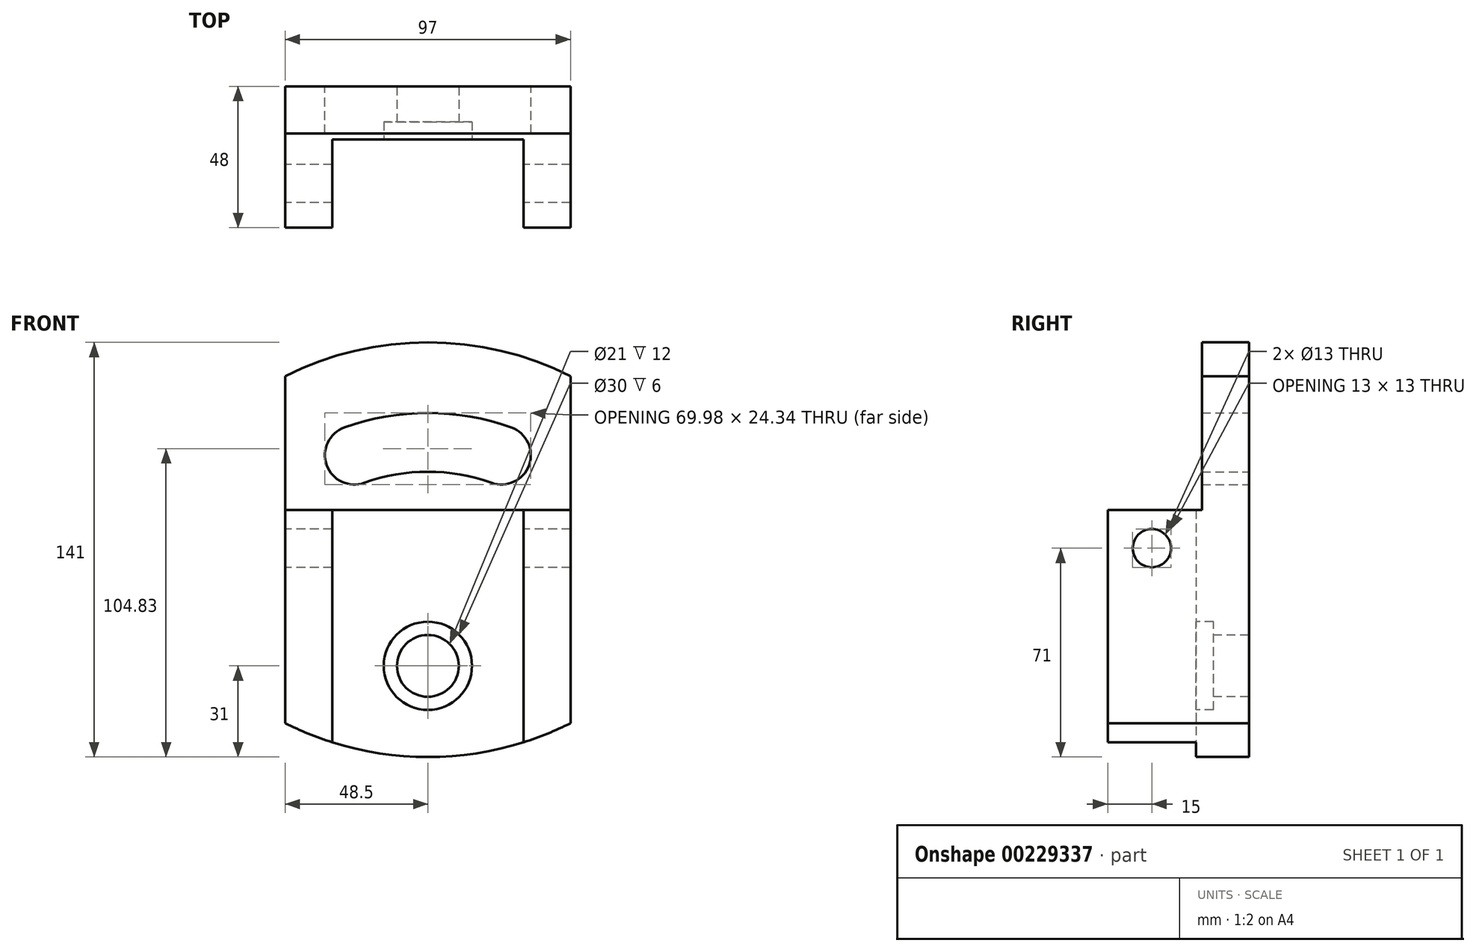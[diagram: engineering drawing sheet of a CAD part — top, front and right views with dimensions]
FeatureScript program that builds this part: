
annotation { "Feature Type Name" : "Feature", "Feature Type Description" : "" }
export const myFeature = defineFeature(function(context is Context, id is Id, definition is map)
    precondition{}
    {
        {
            var Q0;
            Q0=qCreatedBy(makeId("Front.planeOp"),FACE);
            var sketch = newSketch(context, id + "F0", { "sketchPlane" : qUnion([Q0])});
            skLineSegment(sketch, "E0", {"start": v(0, 70.5) * mm, "end": v(0, -70.5) * mm, "construction": true});
            skLineSegment(sketch, "E1", {"start": v(-48.5, 0) * mm, "end": v(48.5, 0) * mm, "construction": true});
            skLineSegment(sketch, "E2.left", {"start": v(48.5, -59) * mm, "end": v(48.5, 59) * mm});
            skLineSegment(sketch, "E2.right", {"start": v(-48.5, -59) * mm, "end": v(-48.5, 59) * mm});
            skPoint(sketch, "E2.middle", {"position": v(0, 0) * mm});
            skArc(sketch, "E3", {"start": v(48.5, 59) * mm, "mid": v(0, 70.5) * mm, "end": v(-48.5, 59) * mm});
            skArc(sketch, "E4", {"start": v(-48.5, -59) * mm, "mid": v(0, -70.5) * mm, "end": v(48.5, -59) * mm});
            skPoint(sketch, "E5.orphan", {"position": v(-48.5, 70.5) * mm});
            skPoint(sketch, "E6.orphan", {"position": v(48.5, 70.5) * mm});
            skPoint(sketch, "E7.orphan", {"position": v(48.5, -70.5) * mm});
            skPoint(sketch, "E2.bottom.end.orphan", {"position": v(-48.5, -70.5) * mm});
            skArc(sketch, "E8.0", {"start": v(25, 32.15) * mm, "mid": v(0, 36.5) * mm, "end": v(-25, 32.15) * mm, "construction": true});
            skArc(sketch, "E9.0.startCap", {"start": v(28.38, 41.56) * mm, "mid": v(34.41, 28.77) * mm, "end": v(21.62, 22.74) * mm});
            skArc(sketch, "E9.0.endCap", {"start": v(-21.62, 22.74) * mm, "mid": v(-34.41, 28.77) * mm, "end": v(-28.38, 41.56) * mm});
            skArc(sketch, "E9.0.left", {"start": v(21.62, 22.74) * mm, "mid": v(0, 26.5) * mm, "end": v(-21.62, 22.74) * mm});
            skArc(sketch, "E9.0.right", {"start": v(28.38, 41.56) * mm, "mid": v(0, 46.5) * mm, "end": v(-28.38, 41.56) * mm});
            skArc(sketch, "E10.0.startCap", {"start": v(28.38, 41.56) * mm, "mid": v(34.41, 28.77) * mm, "end": v(21.62, 22.74) * mm, "construction": true});
            skArc(sketch, "E10.0.endCap", {"start": v(-21.62, 22.74) * mm, "mid": v(-34.41, 28.77) * mm, "end": v(-28.38, 41.56) * mm, "construction": true});
            skArc(sketch, "E10.0.left", {"start": v(21.62, 22.74) * mm, "mid": v(0, 26.5) * mm, "end": v(-21.62, 22.74) * mm, "construction": true});
            skArc(sketch, "E10.0.right", {"start": v(28.38, 41.56) * mm, "mid": v(0, 46.5) * mm, "end": v(-28.38, 41.56) * mm, "construction": true});
            skLineSegment(sketch, "E11", {"start": v(-48.5, 13.5) * mm, "end": v(48.5, 13.5) * mm});
            skSolve(sketch);
        }
        {
            var Q0;
            {var subQ0=sQuery(id+"F0.wireOp",EDGE,"E3");Q0=makeQuery(id+"F0.imprint","IMPRINT",FACE,{"disambiguationData":[TD([[makeQuery(id+"F0.imprint","IMPRINT",EDGE,{"derivedFrom":subQ0}),1.0]])]});}
            extrude(context, id + "F1", {"entities" : qUnion([Q0]), "depth" : 16 * mm});
        }
        {
            var Q0;
            {var subQ0=sQuery(id+"F0.wireOp",EDGE,"E4");Q0=makeQuery(id+"F0.imprint","IMPRINT",FACE,{"disambiguationData":[TD([[makeQuery(id+"F0.imprint","IMPRINT",EDGE,{"derivedFrom":subQ0}),1.0]])]});}
            extrude(context, id + "F2", {"entities" : qUnion([Q0]), "operationType" : NewBodyOperationType.ADD, "depth" : 18 * mm});
        }
        {
            var Q0;
            Q0=makeQuery(id+"F2.opExtrude","CAP_FACE",FACE,{"disambiguationData":[OSD([sQuery(id+"F0.wireOp",EDGE,"E2.left"),sQuery(id+"F0.wireOp",EDGE,"E2.right"),sQuery(id+"F0.wireOp",EDGE,"E4"),sQuery(id+"F0.wireOp",EDGE,"E11")])],"isStart":false});
            var sketch = newSketch(context, id + "F3", { "sketchPlane" : qUnion([Q0])});
            skLineSegment(sketch, "E12", {"start": v(0, 0) * mm, "end": v(0, -70.5) * mm, "construction": true});
            skPoint(sketch, "E13", {"position": v(0, -39.5) * mm});
            skSolve(sketch);
        }
        {
            var Q0;
            Q0=sQuery(id+"F3.wireOp",VERTEX,"E13");
            var Q1;
            Q1=makeQuery(id+"F1.opExtrude","SWEPT_BODY",BODY,{"disambiguationData":[OSD([sQuery(id+"F0.wireOp",EDGE,"E2.left"),sQuery(id+"F0.wireOp",EDGE,"E2.right"),sQuery(id+"F0.wireOp",EDGE,"E3"),sQuery(id+"F0.wireOp",EDGE,"E9.0.startCap"),sQuery(id+"F0.wireOp",EDGE,"E9.0.endCap"),sQuery(id+"F0.wireOp",EDGE,"E9.0.left"),sQuery(id+"F0.wireOp",EDGE,"E9.0.right"),sQuery(id+"F0.wireOp",EDGE,"E11")])]});
            hole(context, id + "F4", {"style" : HoleStyle.C_BORE, "endStyle" : HoleEndStyle.THROUGH, "holeDiameter" : 21 * mm, "cBoreDiameter" : 30 * mm, "cBoreDepth" : 6 * mm, "startFromSketch" : true, "locations" : qUnion([Q0]), "scope" : qUnion([Q1]), "isTappedThrough" : true});
        }
        {
            var Q0;
            Q0=makeQuery(id+"F2.opExtrude","CAP_FACE",FACE,{"disambiguationData":[OSD([sQuery(id+"F0.wireOp",EDGE,"E2.left"),sQuery(id+"F0.wireOp",EDGE,"E2.right"),sQuery(id+"F0.wireOp",EDGE,"E4"),sQuery(id+"F0.wireOp",EDGE,"E11")])],"isStart":false});
            var sketch = newSketch(context, id + "F5", { "sketchPlane" : qUnion([Q0])});
            skLineSegment(sketch, "E14.0", {"start": v(-48.5, -59) * mm, "end": v(-48.5, 13.5) * mm});
            skLineSegment(sketch, "E15.0", {"start": v(-48.5, 13.5) * mm, "end": v(-32.5, 13.5) * mm});
            skLineSegment(sketch, "E16.0", {"start": v(48.5, -59) * mm, "end": v(48.5, 13.5) * mm});
            skArc(sketch, "E17.0", {"start": v(-48.5, -59) * mm, "mid": v(-40.63, -62.57) * mm, "end": v(-32.5, -65.5) * mm});
            skLineSegment(sketch, "E18", {"start": v(-32.5, 13.5) * mm, "end": v(-32.5, -65.5) * mm});
            skLineSegment(sketch, "E19", {"start": v(32.5, 13.5) * mm, "end": v(32.5, -65.5) * mm});
            skArc(sketch, "E20.trimOffspring", {"start": v(32.5, -65.5) * mm, "mid": v(40.63, -62.57) * mm, "end": v(48.5, -59) * mm});
            skLineSegment(sketch, "E21.trimOffspring", {"start": v(32.5, 13.5) * mm, "end": v(48.5, 13.5) * mm});
            skSolve(sketch);
        }
        {
            var Q0;
            Q0 = qSketchRegion(id + "F5", true);
            extrude(context, id + "F6", {"entities" : qUnion([Q0]), "operationType" : NewBodyOperationType.ADD, "depth" : 30 * mm});
        }
        {
            var Q0;
            {var subQ0=sQuery(id+"F0.wireOp",EDGE,"E2.right");Q0=makeQuery(id+"F6.boolean.opBoolean","MERGE",FACE,{"derivedFrom":[makeQuery(id+"F2.boolean.opBoolean","MERGE",FACE,{"derivedFrom":[makeQuery(id+"F1.opExtrude","SWEPT_FACE",FACE,{"disambiguationData":[OSD([subQ0])]}),makeQuery(id+"F2.opExtrude","SWEPT_FACE",FACE,{"disambiguationData":[OSD([subQ0])]})]}),makeQuery(id+"F6.opExtrude","SWEPT_FACE",FACE,{"disambiguationData":[OSD([sQuery(id+"F5.wireOp",EDGE,"E14.0")])]})]});}
            var sketch = newSketch(context, id + "F7", { "sketchPlane" : qUnion([Q0])});
            skPoint(sketch, "E22", {"position": v(33, 0.5) * mm});
            skSolve(sketch);
        }
        {
            var Q0;
            Q0=sQuery(id+"F7.wireOp",VERTEX,"E22");
            var Q1;
            Q1=makeQuery(id+"F1.opExtrude","SWEPT_BODY",BODY,{"disambiguationData":[OSD([sQuery(id+"F0.wireOp",EDGE,"E2.left"),sQuery(id+"F0.wireOp",EDGE,"E2.right"),sQuery(id+"F0.wireOp",EDGE,"E3"),sQuery(id+"F0.wireOp",EDGE,"E9.0.startCap"),sQuery(id+"F0.wireOp",EDGE,"E9.0.endCap"),sQuery(id+"F0.wireOp",EDGE,"E9.0.left"),sQuery(id+"F0.wireOp",EDGE,"E9.0.right"),sQuery(id+"F0.wireOp",EDGE,"E11")])]});
            hole(context, id + "F8", {"style" : HoleStyle.SIMPLE, "endStyle" : HoleEndStyle.THROUGH, "holeDiameter" : 13 * mm, "startFromSketch" : true, "locations" : qUnion([Q0]), "scope" : qUnion([Q1]), "isTappedThrough" : true});
        }
    });
